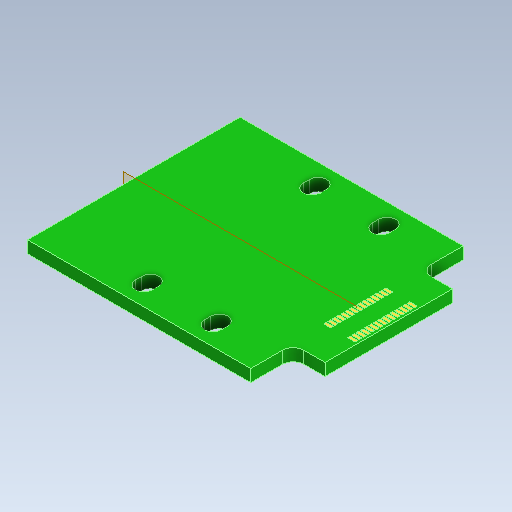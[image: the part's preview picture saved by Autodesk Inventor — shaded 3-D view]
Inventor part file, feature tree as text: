
AUTODESK INVENTOR PART (.ipt)
format: ipt  version: 2021 (Build 250183000, 183)  size: 371,200 bytes
history: native  units: mm
features: extrude x4, sketch x4, plane x1, projected_geometry x1
ambient origin geometry x8: Origin, YZ Plane, XZ Plane, XY Plane, X Axis, Y Axis, Z Axis, Center Point
bodies: Solid1 (feature_tree)
feature tree (10):
  extrude  "Extrusion1"  Depth=40.0mm
  extrude  "Extrusion2"  Depth=2.3mm
  extrude  "Extrusion3"  Depth=3.2mm
  plane  "Work Plane1"
  extrude  "Extrusion4"  Depth=16.7mm
  sketch  "Sketch1"  dims[d0=48.0mm d1=40.0mm]
  sketch  "Sketch2"  dims[d2=2.3mm d3=0.0mm d4=31.6mm]
  sketch  "Sketch3"  dims[d5=3.2mm d6=1.2mm]
  projected_geometry  "Projected Loop1"
  sketch  "Sketch4"  dims[d7=3.2mm d8=1.2mm d9=16.7mm d10=29.7mm d11=0.0mm d12=0.0mm d13=0.5mm d14=1.4mm d15=0.5mm d16=1.3mm d17=0.5mm d18=6.4mm d19=80.0mm d21=0.8mm d22=10.0mm d24=10.0mm d26=80.0mm d28=0.8mm d29=10.0mm d31=10.0mm d33=0.01mm d34=0.0mm d35=6.0mm d36=8.0mm d37=2.0mm d38=0.01mm d39=0.0mm]
